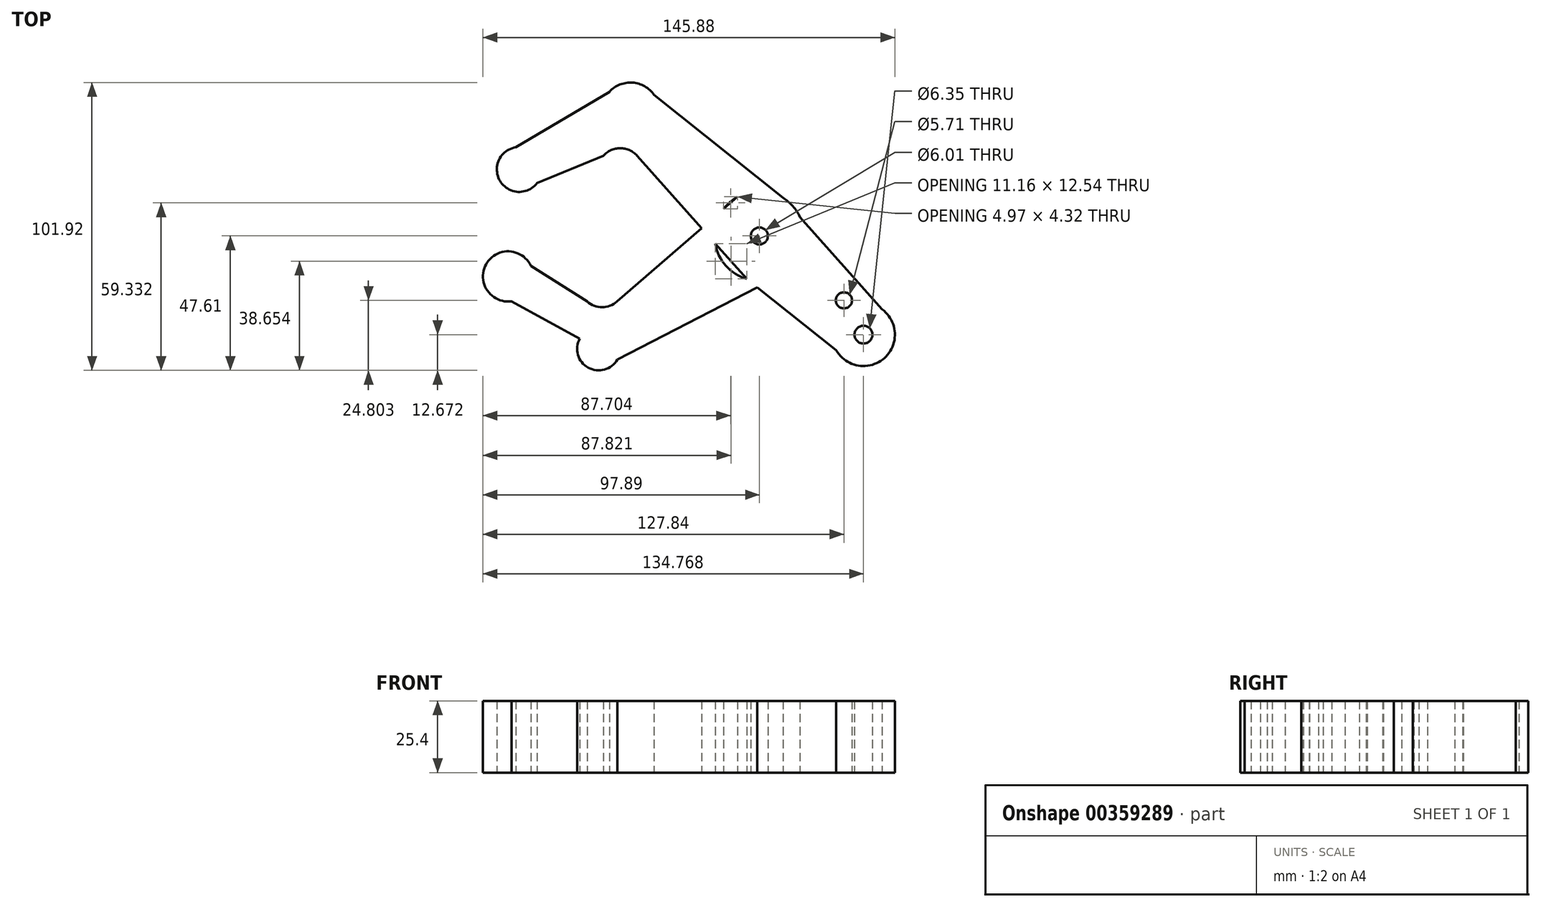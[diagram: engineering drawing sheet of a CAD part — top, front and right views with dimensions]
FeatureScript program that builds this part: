
annotation { "Feature Type Name" : "Feature", "Feature Type Description" : "" }
export const myFeature = defineFeature(function(context is Context, id is Id, definition is map)
    precondition{}
    {
        {
            var Q0;
            Q0=qCreatedBy(makeId("Top.planeOp"),FACE);
            var sketch = newSketch(context, id + "F0", { "sketchPlane" : qUnion([Q0])});
            skCircle(sketch, "E0", {"center": v(0, 0) * mm, "radius": 15.88 * mm});
            skLineSegment(sketch, "E1", {"start": v(-4.5, -15.23) * mm, "end": v(-43.3, 28.4) * mm});
            skLineSegment(sketch, "E2", {"start": v(-4.5, -15.23) * mm, "end": v(27.24, -40.46) * mm});
            skLineSegment(sketch, "E3", {"start": v(8.35, 13.5) * mm, "end": v(46.52, -29.41) * mm});
            skLineSegment(sketch, "E4", {"start": v(7.27, -14.11) * mm, "end": v(-57.66, -47.57) * mm});
            skLineSegment(sketch, "E5", {"start": v(-7.7, 13.88) * mm, "end": v(-50.4, -23.23) * mm});
            skLineSegment(sketch, "E6", {"start": v(-53.1, 51.04) * mm, "end": v(-91.33, 28.36) * mm});
            skLineSegment(sketch, "E7", {"start": v(-55.23, 28.36) * mm, "end": v(-78.72, 18.72) * mm});
            skCircle(sketch, "E8", {"center": v(-45.64, 44.15) * mm, "radius": 10.16 * mm});
            skPoint(sketch, "E8.third.point", {"position": v(-48.64, 34.44) * mm});
            skArc(sketch, "E9", {"start": v(-43.3, 28.4) * mm, "mid": v(-49.28, 31.08) * mm, "end": v(-55.23, 28.36) * mm});
            skCircle(sketch, "E10", {"center": v(-85.03, 23.54) * mm, "radius": 7.94 * mm});
            skPoint(sketch, "E10.third.point", {"position": v(-77.32, 21.66) * mm});
            skCircle(sketch, "E11", {"center": v(36.88, -34.94) * mm, "radius": 11.11 * mm});
            skPoint(sketch, "E11.third.point", {"position": v(46.52, -40.46) * mm});
            skCircle(sketch, "E12", {"center": v(36.88, -34.94) * mm, "radius": 3.18 * mm});
            skLineSegment(sketch, "E13", {"start": v(8.35, 13.5) * mm, "end": v(-37.28, 49.92) * mm});
            skCircle(sketch, "E14", {"center": v(29.95, -22.8) * mm, "radius": 2.86 * mm});
            skCircle(sketch, "E15", {"center": v(0, 0) * mm, "radius": 3 * mm});
            skLineSegment(sketch, "E16", {"start": v(-63.6, -36.34) * mm, "end": v(-97.05, -18.1) * mm});
            skCircle(sketch, "E17", {"center": v(-56.9, -39.99) * mm, "radius": 7.62 * mm});
            skPoint(sketch, "E17.third.point", {"position": v(-50.4, -36.01) * mm});
            skLineSegment(sketch, "E18", {"start": v(-61, -23.18) * mm, "end": v(-80.94, -10.58) * mm});
            skArc(sketch, "E19", {"start": v(-61, -23.18) * mm, "mid": v(-55.71, -25.2) * mm, "end": v(-50.4, -23.23) * mm});
            skCircle(sketch, "E20", {"center": v(-89, -14.34) * mm, "radius": 8.9 * mm});
            skPoint(sketch, "E20.third.point", {"position": v(-81.3, -18.78) * mm});
            skSolve(sketch);
        }
        {
            var Q0;
            Q0 = qSketchRegion(id + "F0", true);
            extrude(context, id + "F1", {"entities" : qUnion([Q0]), "depth" : 25.4 * mm});
        }
    });
